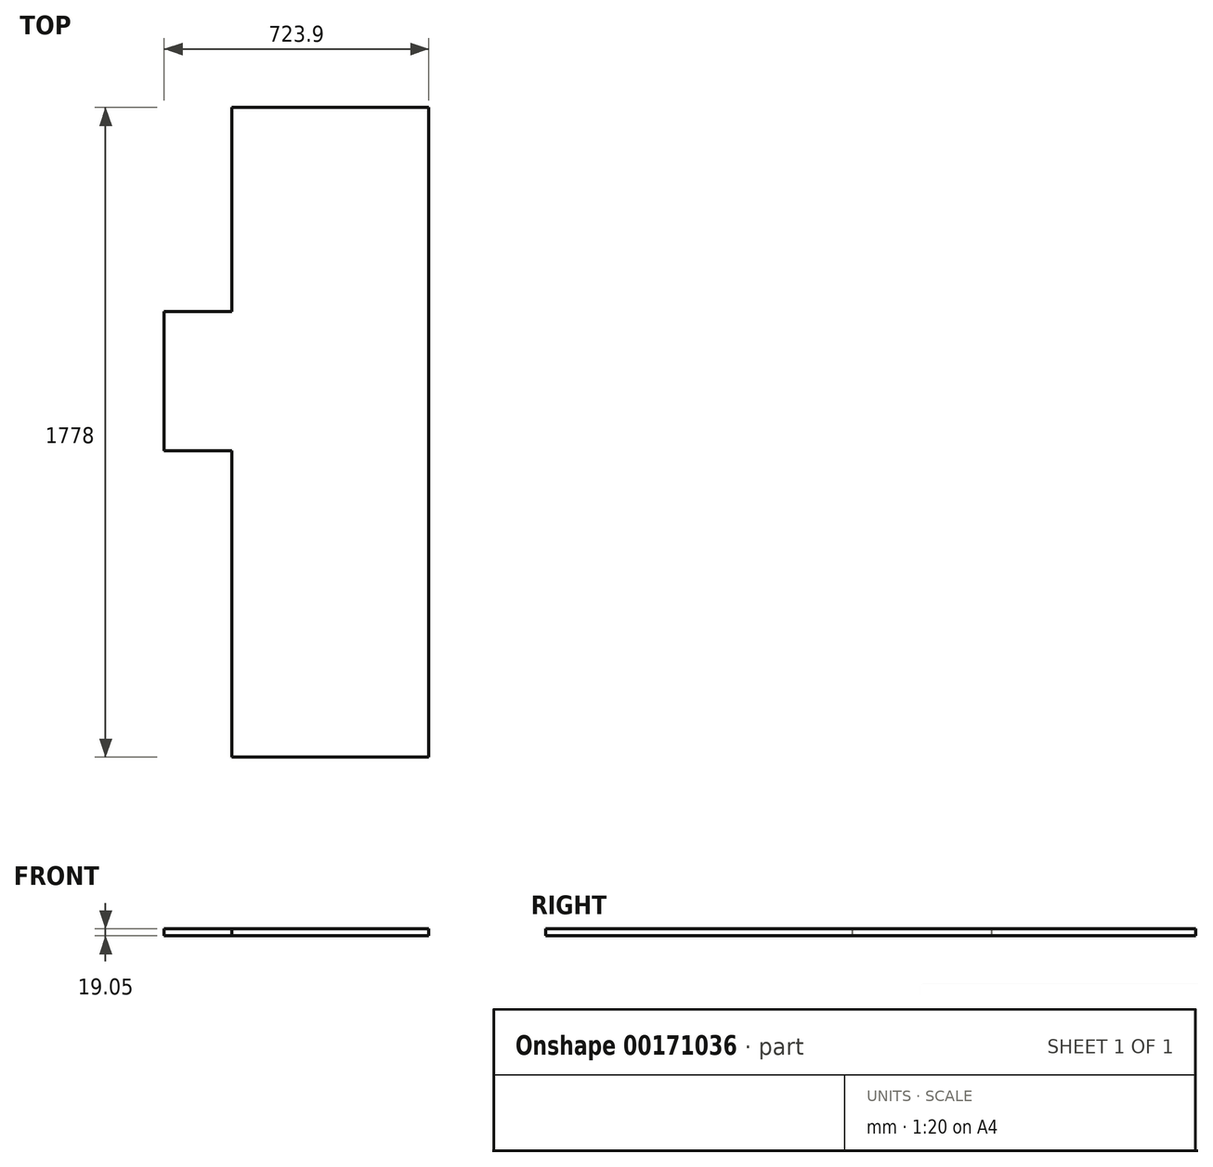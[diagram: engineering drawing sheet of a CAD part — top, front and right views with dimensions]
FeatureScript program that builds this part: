
annotation { "Feature Type Name" : "Feature", "Feature Type Description" : "" }
export const myFeature = defineFeature(function(context is Context, id is Id, definition is map)
    precondition{}
    {
        {
            var Q0;
            Q0=qCreatedBy(makeId("Top.planeOp"),FACE);
            var sketch = newSketch(context, id + "F0", { "sketchPlane" : qUnion([Q0])});
            skLineSegment(sketch, "E0.bottom", {"start": v(0, 889) * mm, "end": v(-538.79, 889) * mm});
            skLineSegment(sketch, "E0.top", {"start": v(0, -889) * mm, "end": v(-538.79, -889) * mm});
            skLineSegment(sketch, "E0.left", {"start": v(0, 889) * mm, "end": v(0, -889) * mm});
            skLineSegment(sketch, "E0.right", {"start": v(-723.9, 330.2) * mm, "end": v(-723.9, -50.8) * mm});
            skLineSegment(sketch, "E1", {"start": v(-723.9, 330.2) * mm, "end": v(-538.79, 330.2) * mm});
            skLineSegment(sketch, "E2", {"start": v(-538.79, 330.2) * mm, "end": v(-538.79, 889) * mm});
            skLineSegment(sketch, "E3", {"start": v(-723.9, -50.8) * mm, "end": v(-538.79, -50.8) * mm});
            skLineSegment(sketch, "E4", {"start": v(-538.79, -50.8) * mm, "end": v(-538.79, -889) * mm});
            skSolve(sketch);
        }
        {
            var Q0;
            Q0=makeQuery(id+"F0.imprint","IMPRINT",FACE,{"disambiguationData":[TD([[makeQuery(id+"F0.imprint","IMPRINT",EDGE,{"derivedFrom":sQuery(id+"F0.wireOp",EDGE,"E0.bottom")}),1.0]])]});
            extrude(context, id + "F1", {"entities" : qUnion([Q0]), "depth" : 19.05 * mm});
        }
    });
